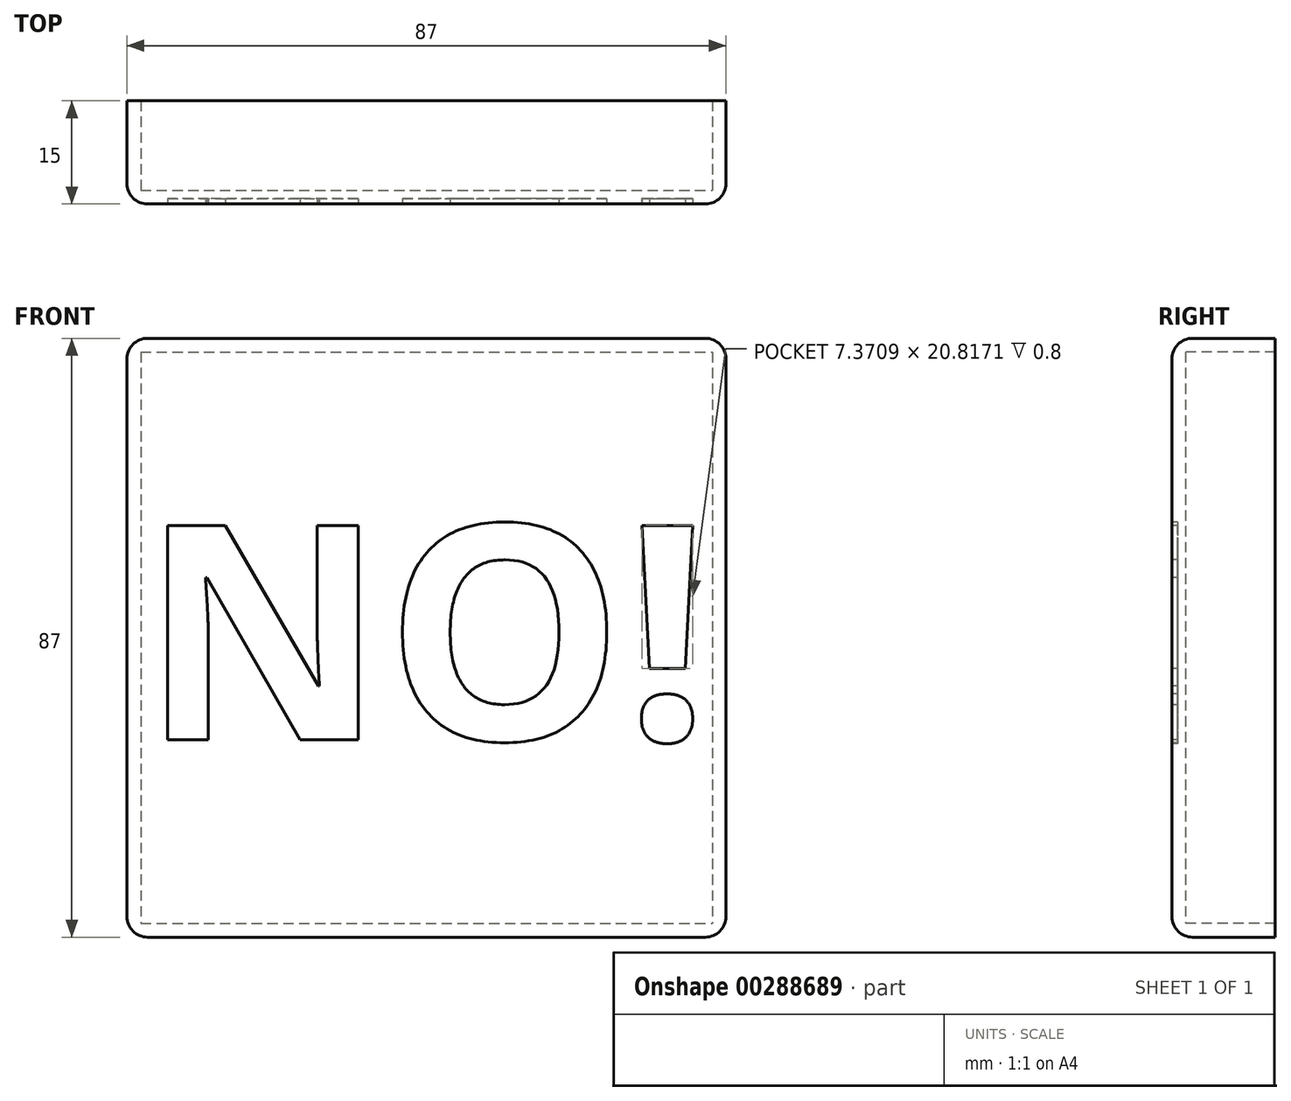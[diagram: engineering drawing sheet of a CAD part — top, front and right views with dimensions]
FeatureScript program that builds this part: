
annotation { "Feature Type Name" : "Feature", "Feature Type Description" : "" }
export const myFeature = defineFeature(function(context is Context, id is Id, definition is map)
    precondition{}
    {
        {
            var Q0;
            Q0=qCreatedBy(makeId("Front.planeOp"),FACE);
            var sketch = newSketch(context, id + "F0", { "sketchPlane" : qUnion([Q0])});
            skLineSegment(sketch, "E0.bottom", {"start": v(-83, 83) * mm, "end": v(0, 83) * mm});
            skLineSegment(sketch, "E0.top", {"start": v(-83, 0) * mm, "end": v(0, 0) * mm});
            skLineSegment(sketch, "E0.left", {"start": v(-83, 83) * mm, "end": v(-83, 0) * mm});
            skLineSegment(sketch, "E0.right", {"start": v(0, 83) * mm, "end": v(0, 0) * mm});
            skLineSegment(sketch, "E1.0", {"start": v(-85, 85) * mm, "end": v(-85, -2) * mm});
            skLineSegment(sketch, "E1.1", {"start": v(-85, 85) * mm, "end": v(2, 85) * mm});
            skLineSegment(sketch, "E1.2", {"start": v(2, 85) * mm, "end": v(2, -2) * mm});
            skLineSegment(sketch, "E1.3", {"start": v(-85, -2) * mm, "end": v(2, -2) * mm});
            skText(sketch, "E2", { "text": "NO!", "fontName": "OpenSans-Bold.ttf"});
            skPoint(sketch, "E3", {"position": v(-41.5, 42.38) * mm});
            skPoint(sketch, "E4", {"position": v(-83, 42.38) * mm});
            skPoint(sketch, "E5", {"position": v(0, 42.38) * mm});
            const initialGuessF0  = {"E2": [-0.083, 0.02667, 1, 0, 0.03142]};
            skSetInitialGuess(sketch, initialGuessF0);
            skSolve(sketch);
        }
        {
            var Q0;
            Q0=makeQuery(id+"F0.imprint","IMPRINT",FACE,{"disambiguationData":[TD([[makeQuery(id+"F0.imprint","IMPRINT",EDGE,{"derivedFrom":sQuery(id+"F0.wireOp",EDGE,"E0.bottom")}),-1.0]])]});
            var Q1;
            Q1=makeQuery(id+"F0.imprint","IMPRINT",FACE,{"disambiguationData":[TD([[makeQuery(id+"F0.imprint","IMPRINT",EDGE,{"derivedFrom":sQuery(id+"F0.wireOp",EDGE,"E0.bottom")}),1.0]])]});
            var Q2;
            Q2=makeQuery(id+"F0.imprint","IMPRINT",FACE,{"disambiguationData":[TD([[makeQuery(id+"F0.imprint","IMPRINT",EDGE,{"derivedFrom":sQuery(id+"F0.wireOp",EDGE,"E2.sketch_text.stroke-22")}),1.0]])]});
            var Q3;
            Q3=makeQuery(id+"F0.imprint","IMPRINT",FACE,{"disambiguationData":[TD([[makeQuery(id+"F0.imprint","IMPRINT",EDGE,{"derivedFrom":sQuery(id+"F0.wireOp",EDGE,"E2.sketch_text.stroke-28")}),-1.0]])]});
            var Q4;
            Q4=makeQuery(id+"F0.imprint","IMPRINT",FACE,{"disambiguationData":[TD([[makeQuery(id+"F0.imprint","IMPRINT",EDGE,{"derivedFrom":sQuery(id+"F0.wireOp",EDGE,"E2.sketch_text.stroke-32")}),-1.0]])]});
            var Q5;
            Q5=makeQuery(id+"F0.imprint","IMPRINT",FACE,{"disambiguationData":[TD([[makeQuery(id+"F0.imprint","IMPRINT",EDGE,{"derivedFrom":sQuery(id+"F0.wireOp",EDGE,"E2.sketch_text.stroke-14")}),-1.0]])]});
            var Q6;
            Q6=makeQuery(id+"F0.imprint","IMPRINT",FACE,{"disambiguationData":[TD([[makeQuery(id+"F0.imprint","IMPRINT",EDGE,{"derivedFrom":sQuery(id+"F0.wireOp",EDGE,"E2.sketch_text.stroke-0")}),-1.0]])]});
            extrude(context, id + "F1", {"entities" : qUnion([Q0, Q1, Q2, Q3, Q4, Q5, Q6]), "oppositeDirection" : true, "depth" : 2 * mm});
        }
        {
            var Q0;
            Q0=makeQuery(id+"F0.imprint","IMPRINT",FACE,{"disambiguationData":[TD([[makeQuery(id+"F0.imprint","IMPRINT",EDGE,{"derivedFrom":sQuery(id+"F0.wireOp",EDGE,"E0.bottom")}),1.0]])]});
            extrude(context, id + "F2", {"entities" : qUnion([Q0]), "operationType" : NewBodyOperationType.ADD, "oppositeDirection" : true, "depth" : 15 * mm});
        }
        {
            var Q0;
            Q0=makeQuery(id+"F0.imprint","IMPRINT",FACE,{"disambiguationData":[TD([[makeQuery(id+"F0.imprint","IMPRINT",EDGE,{"derivedFrom":sQuery(id+"F0.wireOp",EDGE,"E2.sketch_text.stroke-0")}),-1.0]])]});
            var Q1;
            Q1=makeQuery(id+"F0.imprint","IMPRINT",FACE,{"disambiguationData":[TD([[makeQuery(id+"F0.imprint","IMPRINT",EDGE,{"derivedFrom":sQuery(id+"F0.wireOp",EDGE,"E2.sketch_text.stroke-14")}),-1.0]])]});
            var Q2;
            Q2=makeQuery(id+"F0.imprint","IMPRINT",FACE,{"disambiguationData":[TD([[makeQuery(id+"F0.imprint","IMPRINT",EDGE,{"derivedFrom":sQuery(id+"F0.wireOp",EDGE,"E2.sketch_text.stroke-28")}),-1.0]])]});
            var Q3;
            Q3=makeQuery(id+"F0.imprint","IMPRINT",FACE,{"disambiguationData":[TD([[makeQuery(id+"F0.imprint","IMPRINT",EDGE,{"derivedFrom":sQuery(id+"F0.wireOp",EDGE,"E2.sketch_text.stroke-32")}),-1.0]])]});
            extrude(context, id + "F3", {"entities" : qUnion([Q0, Q1, Q2, Q3]), "operationType" : NewBodyOperationType.REMOVE, "oppositeDirection" : true, "depth" : 0.8 * mm});
        }
        {
            var Q0;
            {var subQ0=sQuery(id+"F0.wireOp",EDGE,"E1.3");var subQ1=sQuery(id+"F0.wireOp",EDGE,"E1.2");Q0=makeQuery(id+"F2.boolean.opBoolean","MERGE",EDGE,{"derivedFrom":[makeQuery(id+"F1.opExtrude","SWEPT_EDGE",EDGE,{"disambiguationData":[OSD([subQ1,subQ0])]}),makeQuery(id+"F2.opExtrude","SWEPT_EDGE",EDGE,{"disambiguationData":[OSD([subQ1,subQ0])]})]});}
            var Q1;
            {var subQ0=sQuery(id+"F0.wireOp",EDGE,"E1.3");var subQ1=sQuery(id+"F0.wireOp",EDGE,"E1.0");Q1=makeQuery(id+"F2.boolean.opBoolean","MERGE",EDGE,{"derivedFrom":[makeQuery(id+"F1.opExtrude","SWEPT_EDGE",EDGE,{"disambiguationData":[OSD([subQ1,subQ0])]}),makeQuery(id+"F2.opExtrude","SWEPT_EDGE",EDGE,{"disambiguationData":[OSD([subQ1,subQ0])]})]});}
            var Q2;
            {var subQ0=sQuery(id+"F0.wireOp",EDGE,"E1.1");var subQ1=sQuery(id+"F0.wireOp",EDGE,"E1.0");Q2=makeQuery(id+"F2.boolean.opBoolean","MERGE",EDGE,{"derivedFrom":[makeQuery(id+"F1.opExtrude","SWEPT_EDGE",EDGE,{"disambiguationData":[OSD([subQ1,subQ0])]}),makeQuery(id+"F2.opExtrude","SWEPT_EDGE",EDGE,{"disambiguationData":[OSD([subQ1,subQ0])]})]});}
            var Q3;
            {var subQ0=sQuery(id+"F0.wireOp",EDGE,"E1.2");var subQ1=sQuery(id+"F0.wireOp",EDGE,"E1.1");Q3=makeQuery(id+"F2.boolean.opBoolean","MERGE",EDGE,{"derivedFrom":[makeQuery(id+"F1.opExtrude","SWEPT_EDGE",EDGE,{"disambiguationData":[OSD([subQ1,subQ0])]}),makeQuery(id+"F2.opExtrude","SWEPT_EDGE",EDGE,{"disambiguationData":[OSD([subQ1,subQ0])]})]});}
            fillet(context, id + "F4", {"entities" : qUnion([Q0, Q1, Q2, Q3]), "radius" : 3 * mm, "tangentPropagation" : true, "allowEdgeOverflow" : false});
        }
        {
            var Q0;
            Q0=makeQuery(id+"F1.opExtrude","CAP_EDGE",EDGE,{"disambiguationData":[OSD([sQuery(id+"F0.wireOp",EDGE,"E1.1")])],"isStart":true});
            fillet(context, id + "F5", {"entities" : qUnion([Q0]), "radius" : 3 * mm, "tangentPropagation" : true, "allowEdgeOverflow" : false});
        }
    });
